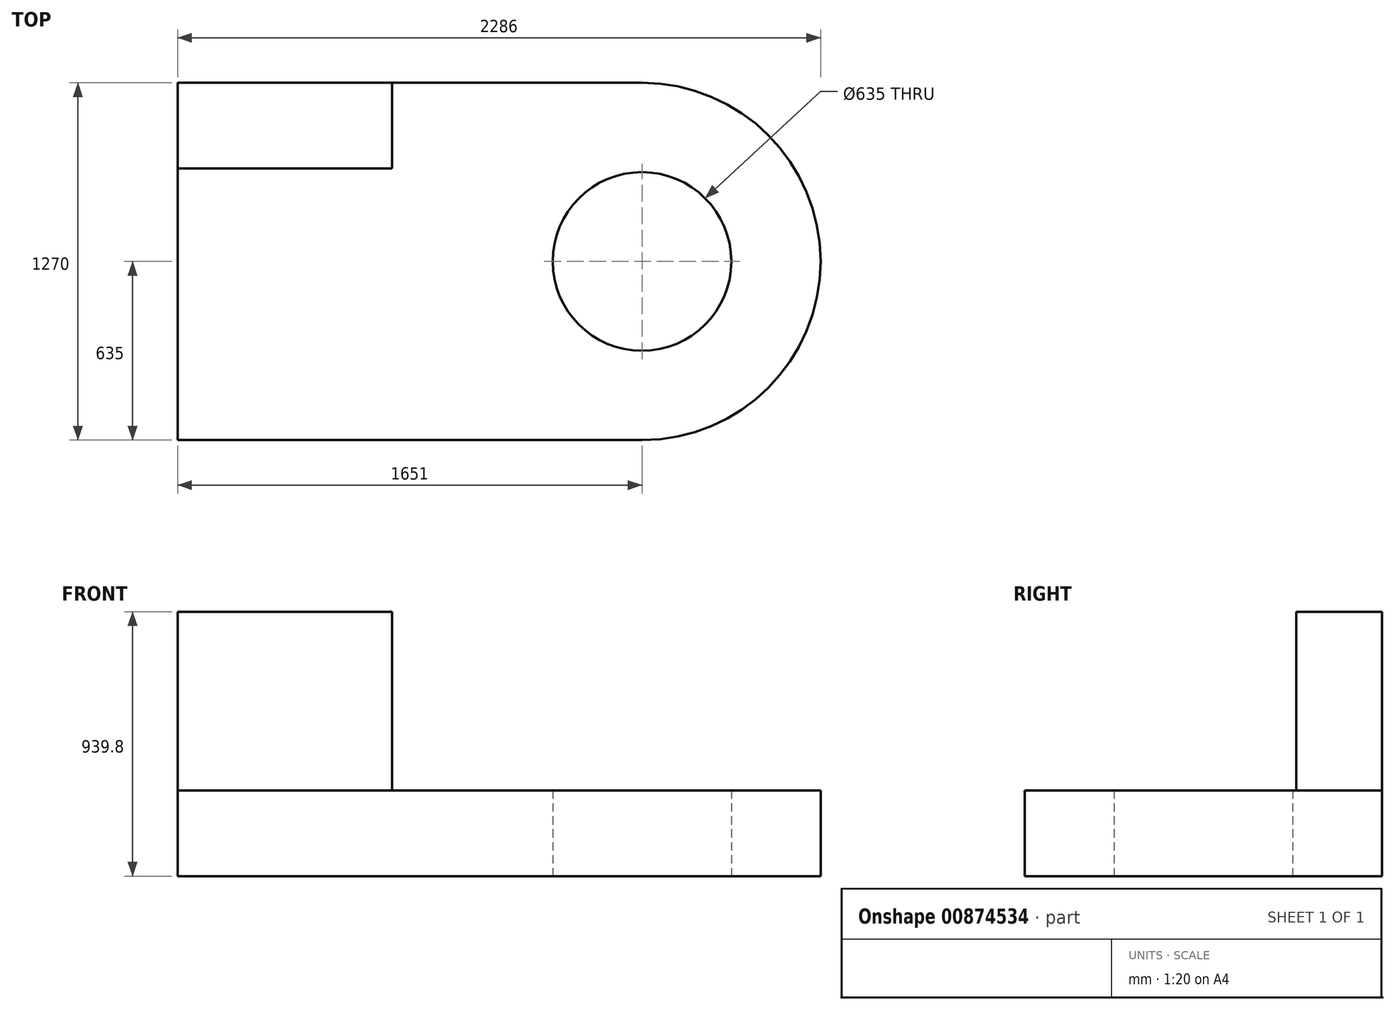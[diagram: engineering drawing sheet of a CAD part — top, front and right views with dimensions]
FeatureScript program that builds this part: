
annotation { "Feature Type Name" : "Feature", "Feature Type Description" : "" }
export const myFeature = defineFeature(function(context is Context, id is Id, definition is map)
    precondition{}
    {
        {
            var Q0;
            Q0=qCreatedBy(makeId("Top.planeOp"),FACE);
            var sketch = newSketch(context, id + "F0", { "sketchPlane" : qUnion([Q0])});
            skLineSegment(sketch, "E0.bottom", {"start": v(0, 0) * mm, "end": v(-1651, 0) * mm});
            skLineSegment(sketch, "E0.top", {"start": v(0, -1270) * mm, "end": v(-1651, -1270) * mm});
            skLineSegment(sketch, "E0.right", {"start": v(-1651, 0) * mm, "end": v(-1651, -1270) * mm});
            skArc(sketch, "E1", {"start": v(0, -1270) * mm, "mid": v(635, -635) * mm, "end": v(0, 0) * mm});
            skCircle(sketch, "E2", {"center": v(0, -635) * mm, "radius": 317.5 * mm});
            skSolve(sketch);
        }
        {
            var Q0;
            Q0=makeQuery(id+"F0.imprint","IMPRINT",FACE,{"disambiguationData":[TD([[makeQuery(id+"F0.imprint","IMPRINT",EDGE,{"derivedFrom":sQuery(id+"F0.wireOp",EDGE,"E0.bottom")}),1.0]])]});
            extrude(context, id + "F1", {"entities" : qUnion([Q0]), "depth" : 304.8 * mm, "offsetDistance" : 25.4 * mm});
        }
        {
            var Q0;
            Q0=makeQuery(id+"F1.opExtrude","CAP_FACE",FACE,{"disambiguationData":[OSD([sQuery(id+"F0.wireOp",EDGE,"E0.bottom"),sQuery(id+"F0.wireOp",EDGE,"E0.top"),sQuery(id+"F0.wireOp",EDGE,"E0.right"),sQuery(id+"F0.wireOp",EDGE,"E1"),sQuery(id+"F0.wireOp",EDGE,"E2")])],"isStart":false});
            var sketch = newSketch(context, id + "F2", { "sketchPlane" : qUnion([Q0])});
            skLineSegment(sketch, "E3.bottom", {"start": v(-1651, 0) * mm, "end": v(-889, 0) * mm});
            skLineSegment(sketch, "E3.top", {"start": v(-1651, -304.8) * mm, "end": v(-889, -304.8) * mm});
            skLineSegment(sketch, "E3.left", {"start": v(-1651, 0) * mm, "end": v(-1651, -304.8) * mm});
            skLineSegment(sketch, "E3.right", {"start": v(-889, 0) * mm, "end": v(-889, -304.8) * mm});
            skSolve(sketch);
        }
        {
            var Q0;
            Q0=makeQuery(id+"F2.imprint","IMPRINT",FACE,{"disambiguationData":[TD([[makeQuery(id+"F2.imprint","IMPRINT",EDGE,{"derivedFrom":sQuery(id+"F2.wireOp",EDGE,"E3.bottom")}),1.0]])]});
            extrude(context, id + "F3", {"entities" : qUnion([Q0]), "operationType" : NewBodyOperationType.ADD, "depth" : 635 * mm, "offsetDistance" : 25.4 * mm});
        }
    });
